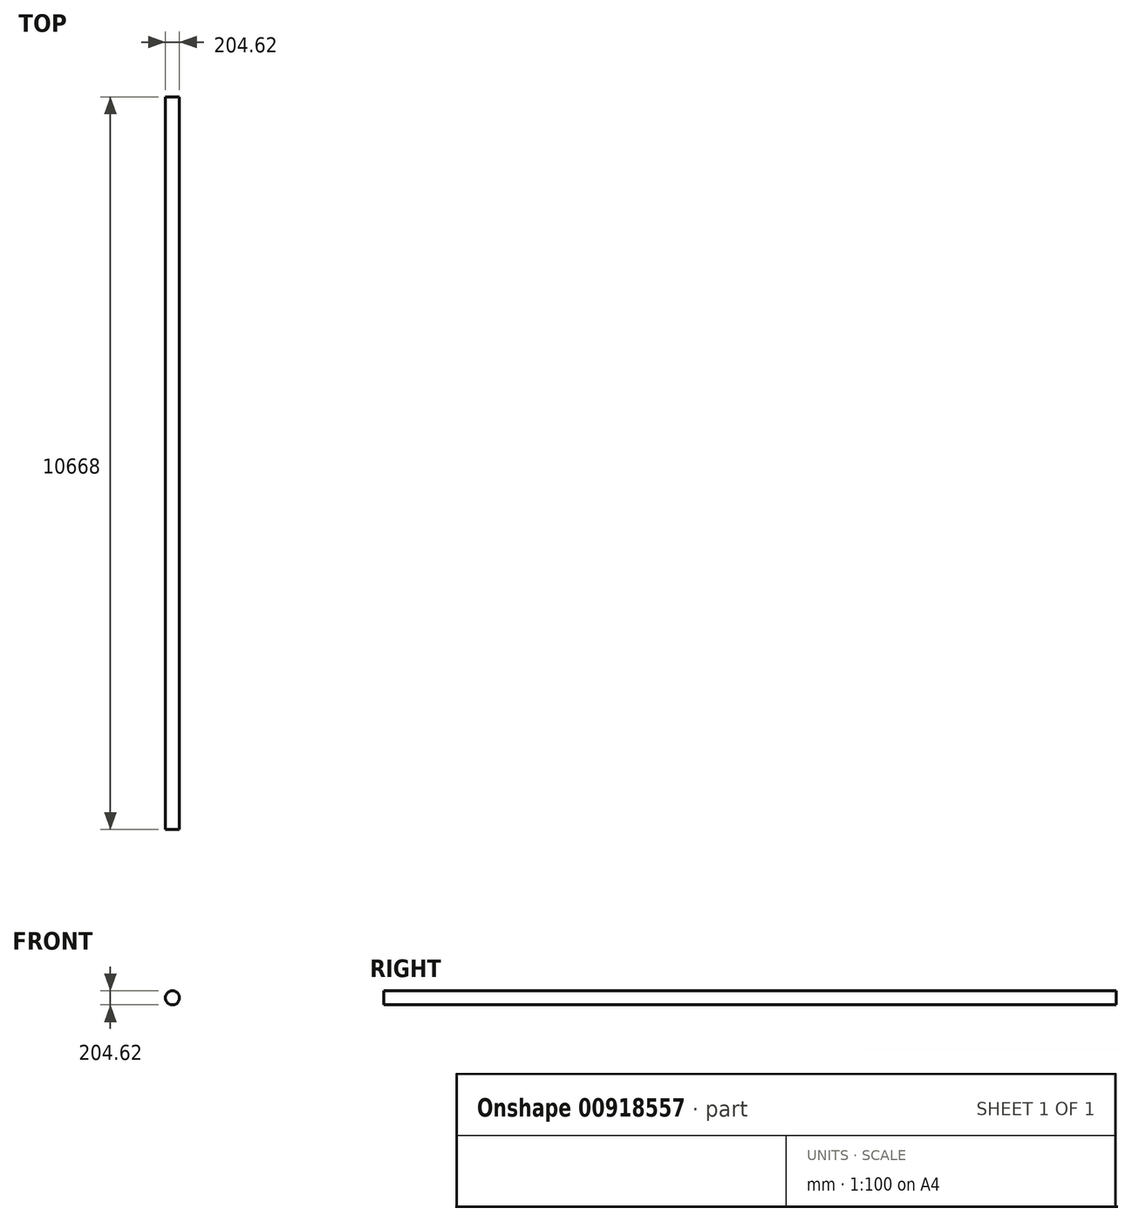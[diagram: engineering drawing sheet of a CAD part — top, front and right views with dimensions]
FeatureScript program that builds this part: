
annotation { "Feature Type Name" : "Feature", "Feature Type Description" : "" }
export const myFeature = defineFeature(function(context is Context, id is Id, definition is map)
    precondition{}
    {
        {
            var Q0;
            Q0=qCreatedBy(makeId("Front.planeOp"),FACE);
            var sketch = newSketch(context, id + "F0", { "sketchPlane" : qUnion([Q0])});
            skCircle(sketch, "E0", {"center": v(0, 0) * mm, "radius": 102.3 * mm});
            skSolve(sketch);
        }
        {
            var Q0;
            Q0=makeQuery(id+"F0.imprint","IMPRINT",FACE,{"disambiguationData":[TD([[makeQuery(id+"F0.imprint","IMPRINT",EDGE,{"derivedFrom":sQuery(id+"F0.wireOp",EDGE,"E0")}),1.0]])]});
            extrude(context, id + "F1", {"entities" : qUnion([Q0]), "depth" : 10668 * mm, "offsetDistance" : 30.48 * mm});
        }
    });
